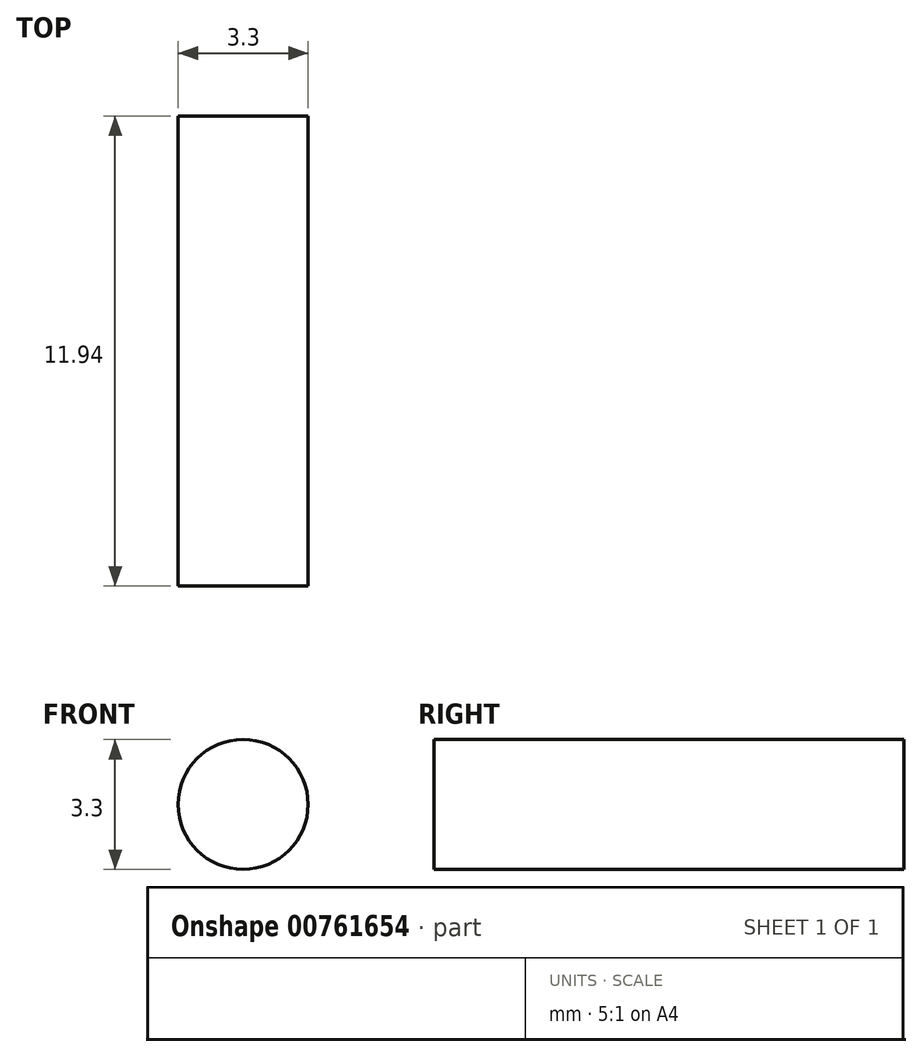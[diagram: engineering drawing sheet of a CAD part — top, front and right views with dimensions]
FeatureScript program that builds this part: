
annotation { "Feature Type Name" : "Feature", "Feature Type Description" : "" }
export const myFeature = defineFeature(function(context is Context, id is Id, definition is map)
    precondition{}
    {
        {
            var Q0;
            Q0=qCreatedBy(makeId("Front.planeOp"),FACE);
            var sketch = newSketch(context, id + "F0", { "sketchPlane" : qUnion([Q0])});
            skCircle(sketch, "E0", {"center": v(0, 0) * mm, "radius": 1.65 * mm});
            skSolve(sketch);
        }
        {
            var Q0;
            Q0 = qSketchRegion(id + "F0", true);
            extrude(context, id + "F1", {"entities" : qUnion([Q0]), "depth" : 11.94 * mm, "offsetDistance" : 25.4 * mm});
        }
    });
